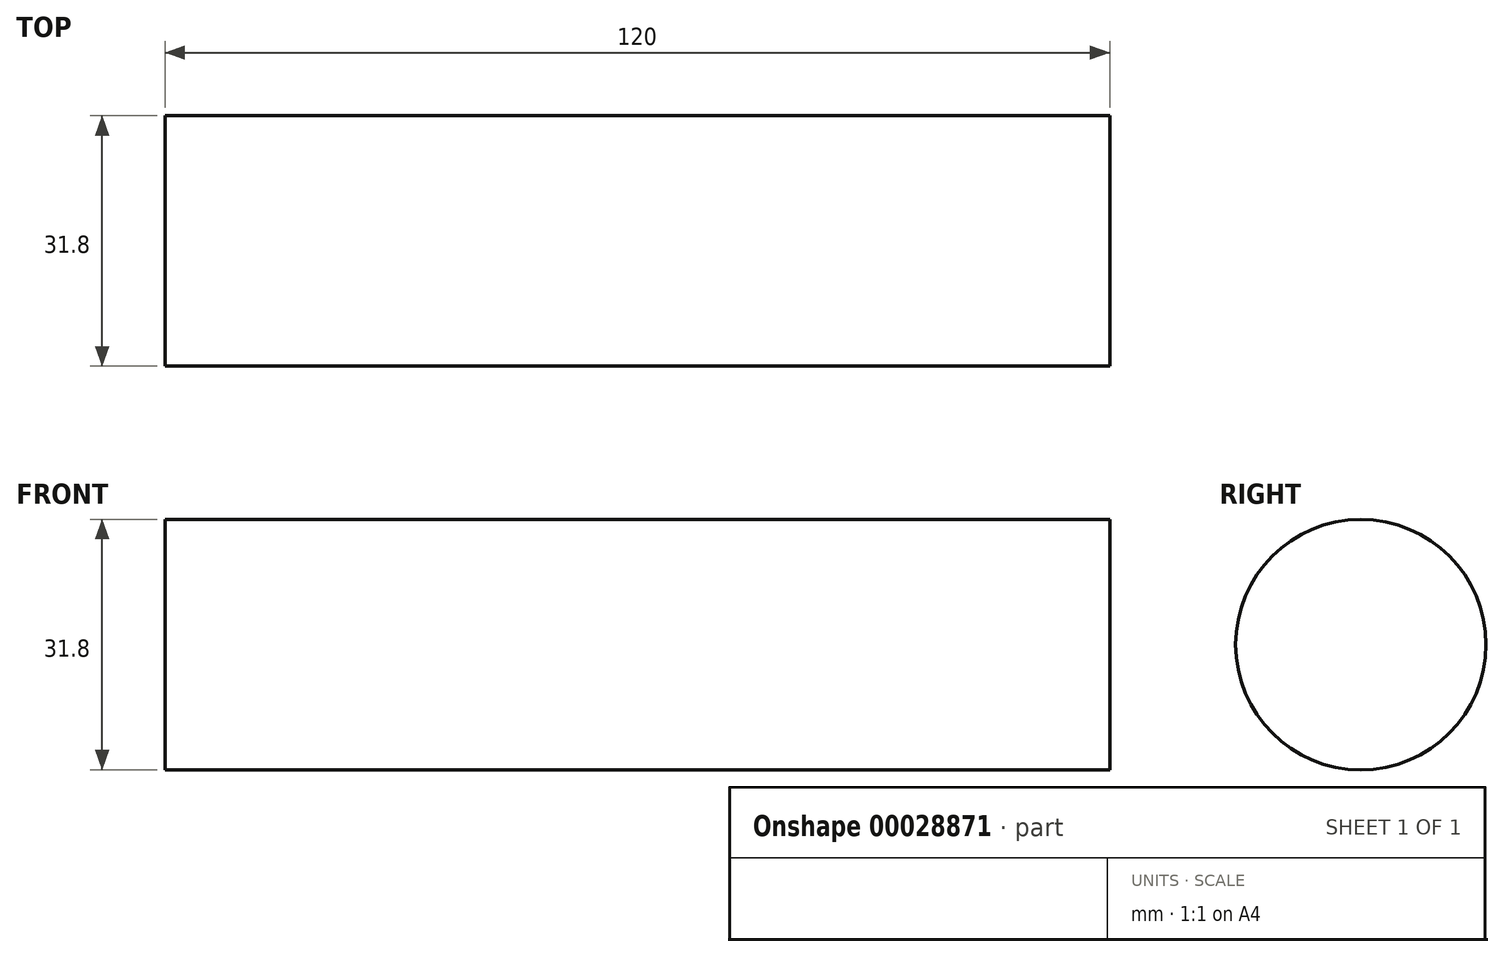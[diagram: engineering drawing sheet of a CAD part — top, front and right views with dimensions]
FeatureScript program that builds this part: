
annotation { "Feature Type Name" : "Feature", "Feature Type Description" : "" }
export const myFeature = defineFeature(function(context is Context, id is Id, definition is map)
    precondition{}
    {
        {
            var Q0;
            Q0=qCreatedBy(makeId("Right.planeOp"),FACE);
            var sketch = newSketch(context, id + "F0", { "sketchPlane" : qUnion([Q0])});
            skCircle(sketch, "E0", {"center": v(0, 0) * mm, "radius": 15.9 * mm});
            skSolve(sketch);
        }
        {
            var Q0;
            Q0 = qSketchRegion(id + "F0", true);
            extrude(context, id + "F1", {"entities" : qUnion([Q0]), "depth" : 60 * mm, "hasSecondDirection" : true, "secondDirectionOppositeDirection" : true, "secondDirectionDepth" : 60 * mm});
        }
    });
